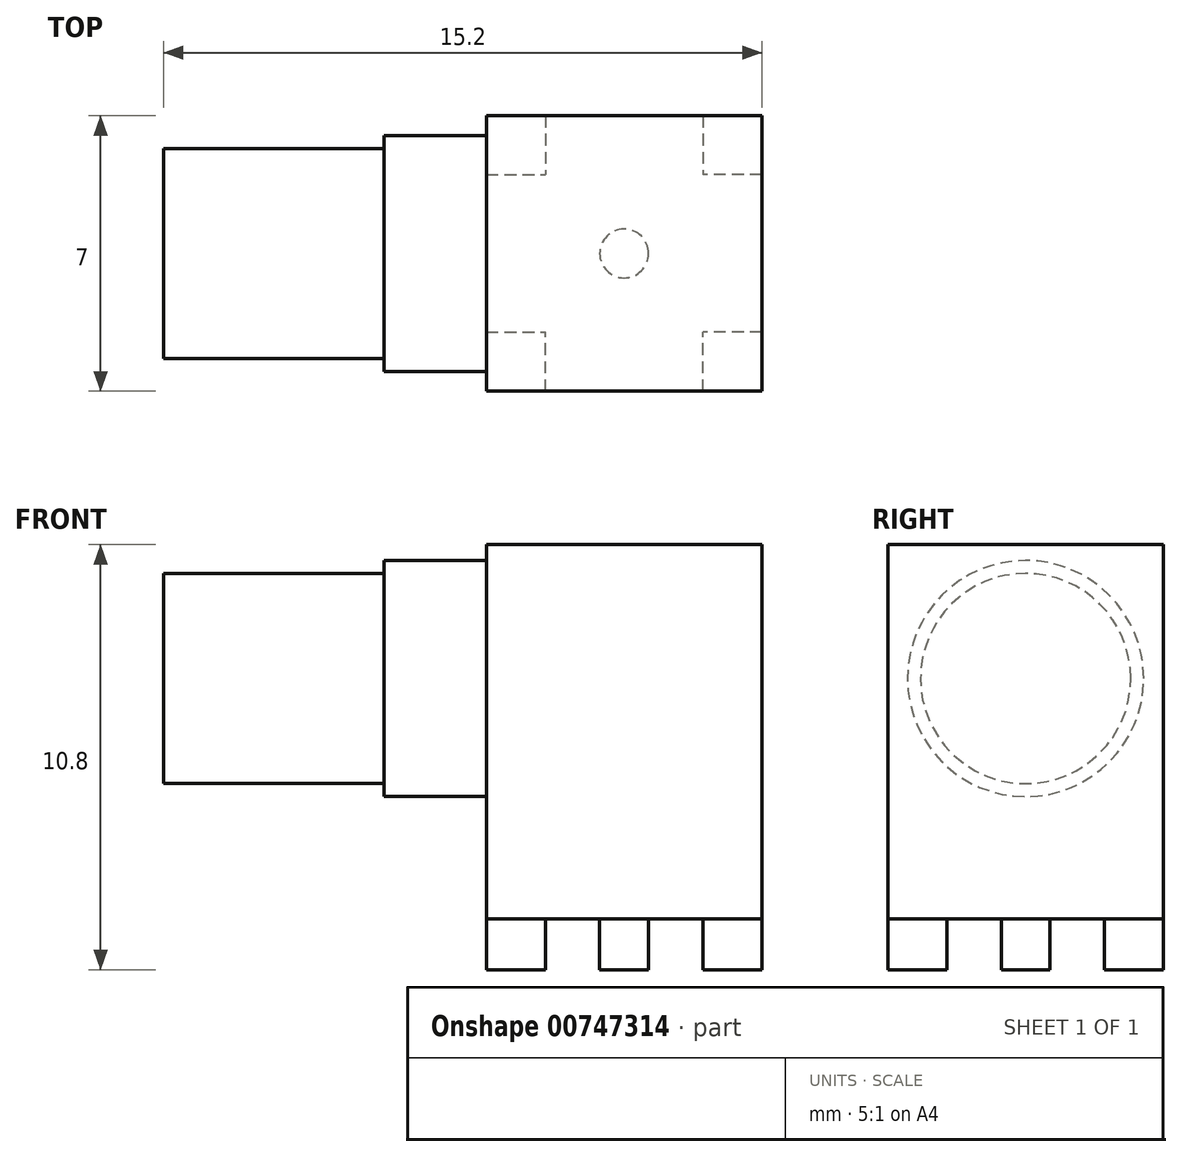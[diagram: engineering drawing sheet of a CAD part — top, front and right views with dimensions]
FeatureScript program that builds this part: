
annotation { "Feature Type Name" : "Feature", "Feature Type Description" : "" }
export const myFeature = defineFeature(function(context is Context, id is Id, definition is map)
    precondition{}
    {
        {
            var Q0;
            Q0=qCreatedBy(makeId("Top.planeOp"),FACE);
            var sketch = newSketch(context, id + "F0", { "sketchPlane" : qUnion([Q0])});
            skLineSegment(sketch, "E0.bottom", {"start": v(0, 7) * mm, "end": v(1.5, 7) * mm});
            skLineSegment(sketch, "E0.top", {"start": v(0, 5.5) * mm, "end": v(1.5, 5.5) * mm});
            skLineSegment(sketch, "E0.left", {"start": v(0, 7) * mm, "end": v(0, 5.5) * mm});
            skLineSegment(sketch, "E0.right", {"start": v(1.5, 7) * mm, "end": v(1.5, 5.5) * mm});
            skLineSegment(sketch, "E1.bottom", {"start": v(7, 7) * mm, "end": v(5.5, 7) * mm});
            skLineSegment(sketch, "E1.top", {"start": v(7, 5.5) * mm, "end": v(5.5, 5.5) * mm});
            skLineSegment(sketch, "E1.left", {"start": v(7, 7) * mm, "end": v(7, 5.5) * mm});
            skLineSegment(sketch, "E1.right", {"start": v(5.5, 7) * mm, "end": v(5.5, 5.5) * mm});
            skLineSegment(sketch, "E2.bottom", {"start": v(7, 0) * mm, "end": v(5.5, 0) * mm});
            skLineSegment(sketch, "E2.top", {"start": v(7, 1.5) * mm, "end": v(5.5, 1.5) * mm});
            skLineSegment(sketch, "E2.left", {"start": v(7, 0) * mm, "end": v(7, 1.5) * mm});
            skLineSegment(sketch, "E2.right", {"start": v(5.5, 0) * mm, "end": v(5.5, 1.5) * mm});
            skLineSegment(sketch, "E3.bottom", {"start": v(0, 0) * mm, "end": v(1.5, 0) * mm});
            skLineSegment(sketch, "E3.top", {"start": v(0, 1.5) * mm, "end": v(1.5, 1.5) * mm});
            skLineSegment(sketch, "E3.left", {"start": v(0, 0) * mm, "end": v(0, 1.5) * mm});
            skLineSegment(sketch, "E3.right", {"start": v(1.5, 0) * mm, "end": v(1.5, 1.5) * mm});
            skCircle(sketch, "E4", {"center": v(3.5, 3.5) * mm, "radius": 0.62 * mm});
            skSolve(sketch);
        }
        {
            var Q0;
            Q0 = qSketchRegion(id + "F0", true);
            extrude(context, id + "F1", {"entities" : qUnion([Q0]), "depth" : 1.3 * mm, "offsetDistance" : 25 * mm});
        }
        {
            var Q0;
            Q0=qCreatedBy(makeId("Top.planeOp"),FACE);
            cPlane(context, id + "F2", {"entities" : qUnion([Q0]), "cplaneType" : CPlaneType.OFFSET, "offset" : 1.3 * mm, "width" : 150 * mm, "height" : 150 * mm});
        }
        {
            var Q0;
            Q0=qCreatedBy(id+"F2.planeOp",FACE);
            var sketch = newSketch(context, id + "F3", { "sketchPlane" : qUnion([Q0])});
            skLineSegment(sketch, "E5.bottom", {"start": v(0, 0) * mm, "end": v(7, 0) * mm});
            skLineSegment(sketch, "E5.top", {"start": v(0, 7) * mm, "end": v(7, 7) * mm});
            skLineSegment(sketch, "E5.left", {"start": v(0, 0) * mm, "end": v(0, 7) * mm});
            skLineSegment(sketch, "E5.right", {"start": v(7, 0) * mm, "end": v(7, 7) * mm});
            skSolve(sketch);
        }
        {
            var Q0;
            Q0 = qSketchRegion(id + "F3", true);
            extrude(context, id + "F4", {"entities" : qUnion([Q0]), "depth" : 9.5 * mm, "offsetDistance" : 25 * mm});
        }
        {
            var Q0;
            Q0=qCreatedBy(makeId("Right.planeOp"),FACE);
            var sketch = newSketch(context, id + "F5", { "sketchPlane" : qUnion([Q0])});
            skCircle(sketch, "E6", {"center": v(3.5, 7.4) * mm, "radius": 3 * mm});
            skSolve(sketch);
        }
        {
            var Q0;
            Q0 = qSketchRegion(id + "F5", true);
            extrude(context, id + "F6", {"entities" : qUnion([Q0]), "operationType" : NewBodyOperationType.ADD, "oppositeDirection" : true, "depth" : 2.6 * mm, "offsetDistance" : 25 * mm});
        }
        {
            var Q0;
            Q0=qCreatedBy(makeId("Right.planeOp"),FACE);
            cPlane(context, id + "F7", {"entities" : qUnion([Q0]), "cplaneType" : CPlaneType.OFFSET, "offset" : 2.6 * mm, "oppositeDirection" : true, "width" : 150 * mm, "height" : 150 * mm});
        }
        {
            var Q0;
            Q0=qCreatedBy(id+"F7.planeOp",FACE);
            var sketch = newSketch(context, id + "F8", { "sketchPlane" : qUnion([Q0])});
            skCircle(sketch, "E7", {"center": v(3.5, 7.4) * mm, "radius": 2.67 * mm});
            skSolve(sketch);
        }
        {
            var Q0;
            Q0 = qSketchRegion(id + "F8", true);
            extrude(context, id + "F9", {"entities" : qUnion([Q0]), "operationType" : NewBodyOperationType.ADD, "oppositeDirection" : true, "depth" : 5.6 * mm, "offsetDistance" : 25 * mm});
        }
    });
